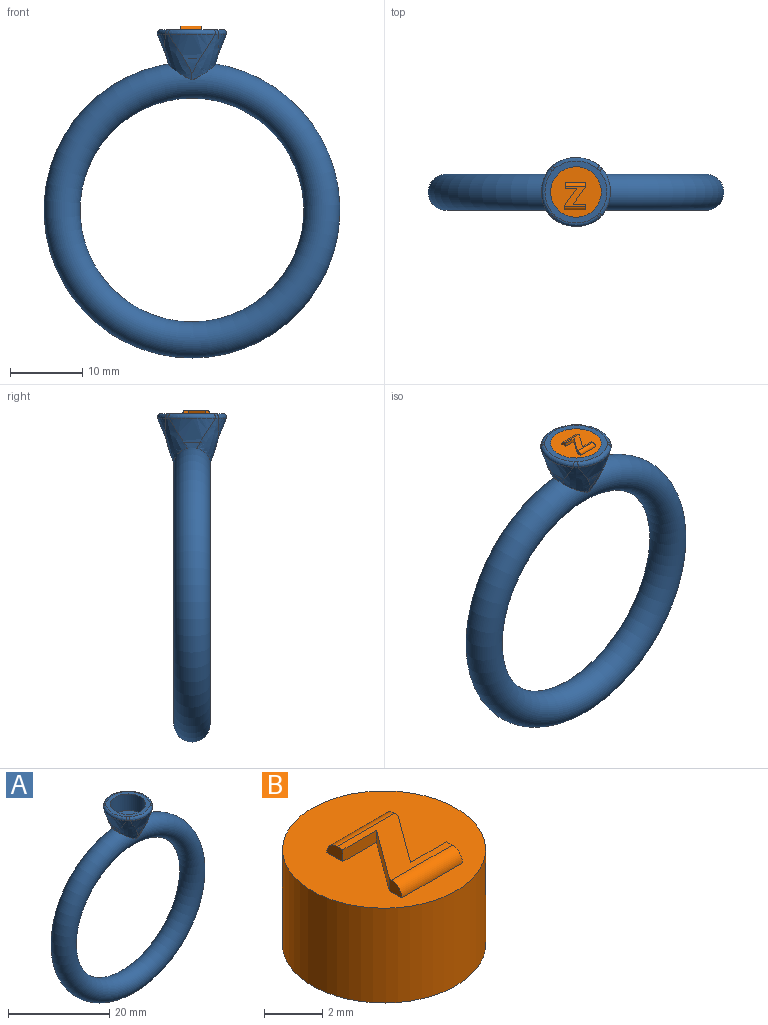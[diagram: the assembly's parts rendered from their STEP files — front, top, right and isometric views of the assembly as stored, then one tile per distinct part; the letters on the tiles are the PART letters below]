
ASSEMBLY  parts=2 mates=1
PART A: 20 faces, bbox 44.4x10x47.2 mm
  f0: torus R=18mm, axis (0,-1,0), area 1747.7mm2, adj f2,f4,f6,f7,f8,f9
  f1: plane 8.59x8.59mm, normal (0,0,1), area 20.2mm2, adj f10,f12,f13,f14,f15,f16,f17,f18
  f2: bspline ~7.07x7mm, area 17.4mm2, adj f0,f6,f8,f16
  f3: bspline ~7.07x7mm, area 18.1mm2, adj f8,f9,f12
  f4: bspline ~7.07x7mm, area 17.4mm2, adj f0,f7,f9,f15
  f5: bspline ~7.07x7mm, area 18.1mm2, adj f6,f7,f19
  f6: bspline ~7.74x4.16mm, area 16mm2, adj f0,f2,f5,f7,f18
  f7: bspline ~7.74x4.16mm, area 16mm2, adj f0,f4,f5,f6,f17
  f8: bspline ~7.74x4.16mm, area 16mm2, adj f0,f2,f3,f9,f14
  f9: bspline ~7.74x4.16mm, area 16mm2, adj f0,f3,f4,f8,f13
  f10: cylinder r=3.5mm len=7mm, axis (0,0,1), area 88mm2, adj f1,f11
  f11: plane 7x7mm, normal (0,0,1), area 38.5mm2, adj f10
  f12: bspline ~7.18x1.97mm, area 6.3mm2, adj f1,f3,f13,f14
  f13: bspline ~1.67x1.67mm, area 0.5mm2, adj f1,f9,f12,f15
  f14: bspline ~1.4x1.31mm, area 0.5mm2, adj f1,f8,f12,f16
  f15: bspline ~7.18x1.97mm, area 6.3mm2, adj f1,f4,f13,f17
  f16: bspline ~7.18x1.97mm, area 6.3mm2, adj f1,f2,f14,f18
  f17: bspline ~1.67x1.67mm, area 0.5mm2, adj f1,f7,f15,f19
  f18: bspline ~1.67x1.67mm, area 0.5mm2, adj f1,f6,f16,f19
  f19: bspline ~7.18x1.97mm, area 6.3mm2, adj f1,f5,f17,f18
PART B: 14 faces, bbox 7x7x4.5 mm
  f0: cylinder r=3.5mm len=7mm, axis (0,0,-1), area 88mm2, adj f1,f2
  f1: plane 7x7mm, normal (0,0,1), area 31.6mm2, adj f0,f4,f5,f6,f7,f8,f9,f10
  f2: plane 7x7mm, normal (0,0,-1), area 38.5mm2, adj f0
  f3: plane 2.96x2.75mm, normal (0,0,1), area 4mm2, adj f4,f5,f6,f7,f8,f9,f10,f11
  f4: plane 0.6x0.5mm, normal (-1,0,0), area 0.2mm2, adj f1,f3,f5,f13
  f5: plane 2.36x1.74mm, normal (-0.81,0.59,0), area 1.5mm2, adj f1,f3,f4,f6
  f6: plane 1.63x0.5mm, normal (0,-1,0), area 0.8mm2, adj f1,f3,f5,f7
  f7: plane 0.78x0.5mm, normal (-1,0,0), area 0.3mm2, adj f1,f3,f6,f12
  f8: plane 0.66x0.5mm, normal (1,0,0), area 0.3mm2, adj f1,f3,f9,f12
  f9: plane 2.3x1.69mm, normal (0.81,-0.59,0), area 1.4mm2, adj f1,f3,f8,f10
  f10: plane 1.75x0.5mm, normal (0,1,0), area 0.9mm2, adj f1,f3,f9,f11
  f11: plane 0.78x0.5mm, normal (1,0,0), area 0.3mm2, adj f1,f3,f10,f13
  f12: cylinder r=0.5mm len=2.8mm, axis (1,0,0), area 2.2mm2, adj f1,f3,f7,f8
  f13: cylinder r=0.5mm len=2.96mm, axis (-1,0,0), area 2.3mm2, adj f1,f3,f4,f11
PLACE A t=(-0.28,0.61,0.39)mm
PLACE B t=(-0.28,0.61,21.39)mm
MATE fastened A.f10 <-> B.f0  axis (0,0,1) through (-0.28,0.61,21.39)mm
